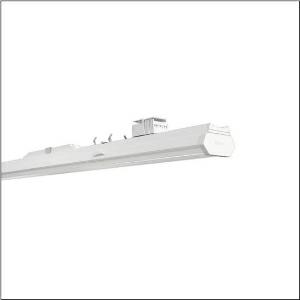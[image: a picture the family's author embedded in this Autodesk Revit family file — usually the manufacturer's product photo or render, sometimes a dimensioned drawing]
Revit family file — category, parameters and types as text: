
# Revit family: licross_r__11_protected_mo_51tp127n58xf_03c6
name_source: partatom
category: Lighting Fixtures
units: mm (PartAtom-declared; Revit-internal decimal feet)

## family parameters
Cut with Voids When Loaded = No
Host = Face
Light Source = No
Part Type = Normal
Room Calculation Point = No
Round Connector Dimension = Use Diameter
Shared = No

## types (1)
- Licross® 11 Protected MO (1 x LED, 8120 lm, 47.6 W, 5000K)
    Apparent Load = 48 VA
    CIE Flux Codes = 73 92 98 99 100
    Color Rendering = 80
    Color Temperature = 5000K
    Default Elevation = 1800 mm
    Description = Licross® 11 Protected MO, luminaire insert, of sheet steel, galvanised, coil coated, white, length: 1.500mm, width: 90mm, height: 101mm, LED rated luminous flux: 8.120lm, light colour: 850, control gear: ON/OFF, control gear: ECG, with plug, 3-pole, with phase selection, mains connection: 220..240V, AC, 50/60Hz, rated input power: 48W, internal wiring halogen-free, primary optical cover: cover, of PMMA, light emission: direct distribution, primary light characteristic: symmetric, protection rating (complete): IP64, insulation class (complete): insulation class I (protective earthing), certification: CE, ENEC, VDE, UKCA, protection symbol: D if used in an environment with conductive dust loads with corresponding accessories, impact resistance: IK06, permissible ambient temperature for indoor applications: -35..+45°C, reducing of maximum allowable ambient temperature of 5°C with ceiling mounting, corresponds to IFS (International Featured Standards) requirements for safety and quality in the food industry, LABS conformity tested according to VDMA 24364:2018-05, packaging unit: 1 piece
    Height = 92 mm
    Lamp = 1 x LED
    Lamp Light Flux = 8120 lm
    Lamp Power = 47.6 W
    Lamp count = 1
    Length = 1500 mm
    Luminous efficacy = 171 lm/W
    Manufacturer = Siteco
    ModVariant = No
    Model = 51TP127N58XF
    Mounting Place = Ceiling
    Mounting Type = Pendant
    Number of Poles = 1
    OnlyDefault = Yes
    Power Factor = 1
    Product Name = Licross® 11 Protected MO
    Product group = luminaire insert | ceiling pendant
    ProductGroupID = 902
    Protection Class = Protection class I
    Protection Degree = IP 64
    RLX_Detail_Level = 1
    RLX_Emergency_Light_Flux = 0 lm
    RLX_Emergency_Type = 0
    RLX_Emergency_Type_DB = No
    RlxData = <blob elided: 20661 chars, md5=c8812849>
    Socket = socket
    Standby Power = 0 W
    System Light Flux = 8120 lm
    System Power = 48 W
    Type Comments = Product without accessories
    Type Image = l_1256148.jpg
    URL = http://relux.com
    VarID = ---
    Voltage = 0 V
    Weight = 0.00 kg
    Width = 88 mm

## geometry (parser evidence)
native form markers: Blend x4, Sweep x12
no freeform markers — native parametric forms only
